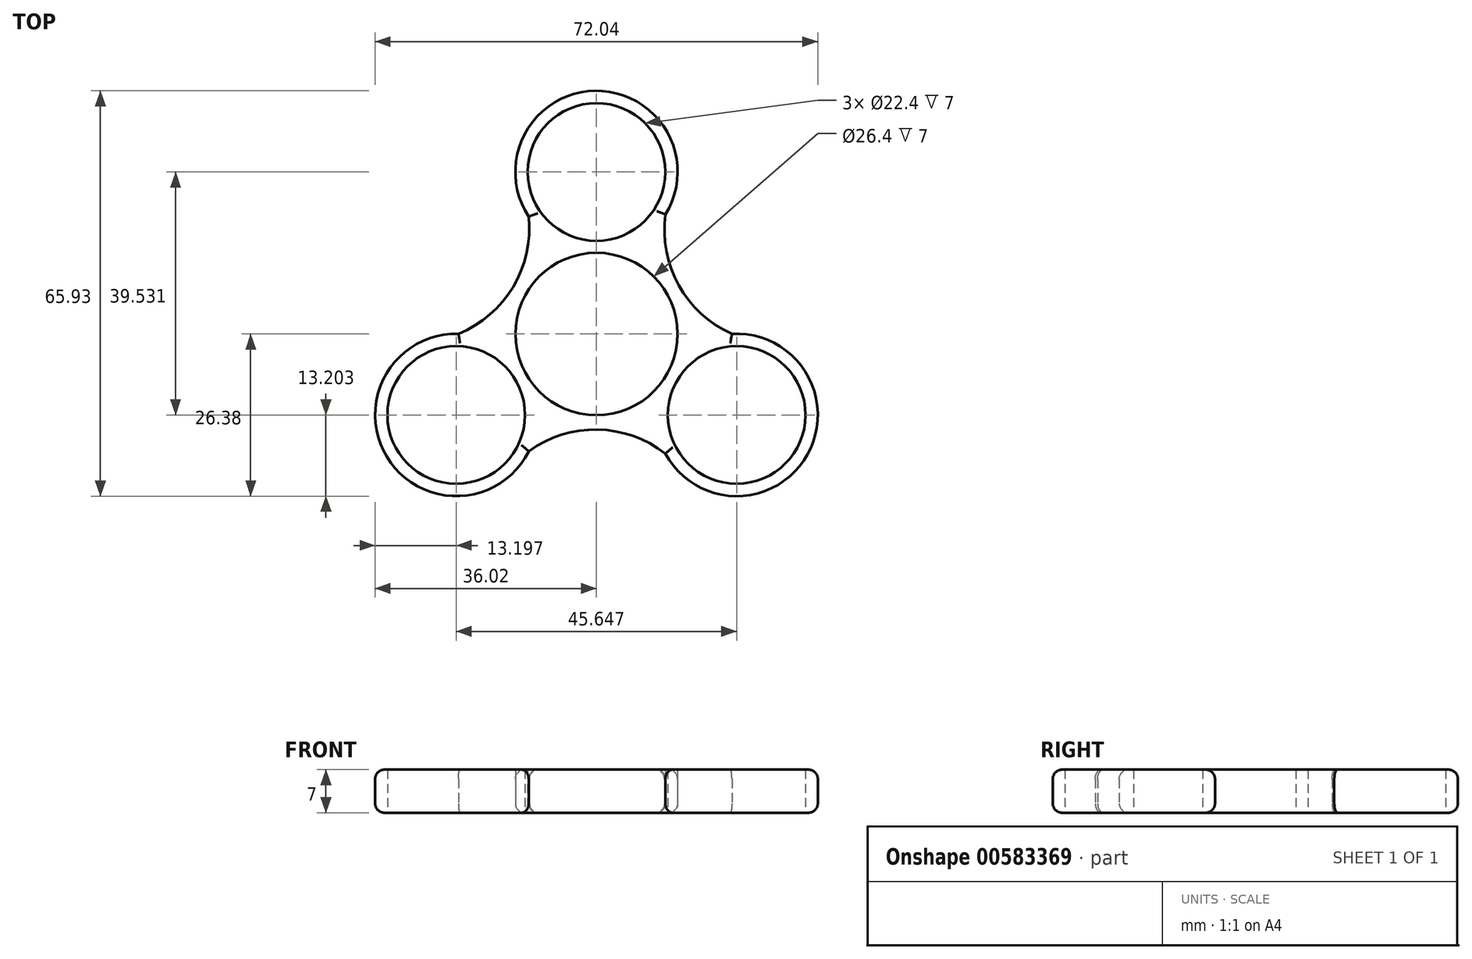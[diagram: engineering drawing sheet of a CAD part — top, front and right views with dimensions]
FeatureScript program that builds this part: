
annotation { "Feature Type Name" : "Feature", "Feature Type Description" : "" }
export const myFeature = defineFeature(function(context is Context, id is Id, definition is map)
    precondition{}
    {
        {
            var Q0;
            Q0=qCreatedBy(makeId("Top.planeOp"),FACE);
            var sketch = newSketch(context, id + "F0", { "sketchPlane" : qUnion([Q0])});
            skCircle(sketch, "E0", {"center": v(0, 0) * mm, "radius": 11.2 * mm});
            skCircle(sketch, "E1", {"center": v(0, 0) * mm, "radius": 13.2 * mm});
            skCircle(sketch, "E2", {"center": v(0, 26.35) * mm, "radius": 11.2 * mm});
            skArc(sketch, "E3", {"start": v(11.25, 19.44) * mm, "mid": v(-0.2, 39.55) * mm, "end": v(-11.02, 19.1) * mm});
            skArc(sketch, "E4.1.0", {"start": v(-22.46, 0.02) * mm, "mid": v(-34.15, -19.96) * mm, "end": v(-11.02, -19.1) * mm});
            skCircle(sketch, "E4.1.1", {"center": v(-22.82, -13.18) * mm, "radius": 11.2 * mm});
            skArc(sketch, "E4.2.0", {"start": v(11.8, -5.91) * mm, "mid": v(11.4, -6.58) * mm, "end": v(11.02, -7.26) * mm});
            skCircle(sketch, "E4.2.1", {"center": v(22.82, -13.18) * mm, "radius": 11.2 * mm});
            skLineSegment(sketch, "E5", {"start": v(-11.4, -6.64) * mm, "end": v(-11.37, -6.62) * mm});
            skArc(sketch, "E6", {"start": v(11.25, 19.44) * mm, "mid": v(13.4, 7.92) * mm, "end": v(22.04, 0) * mm});
            skArc(sketch, "E7.1.0", {"start": v(-22.46, 0.02) * mm, "mid": v(-13.56, 7.64) * mm, "end": v(-11.02, 19.1) * mm});
            skArc(sketch, "E7.2.0", {"start": v(11.22, -19.46) * mm, "mid": v(0.16, -15.56) * mm, "end": v(-11.02, -19.1) * mm});
            skArc(sketch, "E8.trimOffspring", {"start": v(11.22, -19.46) * mm, "mid": v(34.36, -19.6) * mm, "end": v(22.04, 0) * mm});
            skPoint(sketch, "E9.orphan", {"position": v(46.18, 26.35) * mm});
            skLineSegment(sketch, "E10.trimOffspring", {"start": v(11.48, 6.47) * mm, "end": v(11.5, 6.49) * mm});
            skArc(sketch, "E11.trimOffspring", {"start": v(-11.02, -7.26) * mm, "mid": v(-11.4, -6.58) * mm, "end": v(-11.8, -5.91) * mm});
            skLineSegment(sketch, "E12.trimOffspring", {"start": v(11.02, 7.26) * mm, "end": v(11.8, 5.91) * mm});
            skSolve(sketch);
        }
        {
            var Q0;
            Q0=makeQuery(id+"F0.imprint","IMPRINT",FACE,{"disambiguationData":[TD([[makeQuery(id+"F0.imprint","IMPRINT",EDGE,{"derivedFrom":sQuery(id+"F0.wireOp",EDGE,"E2")}),-1.0]])]});
            extrude(context, id + "F1", {"entities" : qUnion([Q0]), "depth" : 7 * mm, "offsetDistance" : 25 * mm});
        }
        {
            var Q0;
            Q0=makeQuery(id+"F1.opExtrude","CAP_EDGE",EDGE,{"disambiguationData":[OSD([sQuery(id+"F0.wireOp",EDGE,"E7.2.0")])],"isStart":false});
            var Q1;
            Q1=makeQuery(id+"F1.opExtrude","CAP_EDGE",EDGE,{"disambiguationData":[OSD([sQuery(id+"F0.wireOp",EDGE,"E4.1.0")])],"isStart":false});
            var Q2;
            Q2=makeQuery(id+"F1.opExtrude","CAP_EDGE",EDGE,{"disambiguationData":[OSD([sQuery(id+"F0.wireOp",EDGE,"E7.1.0")])],"isStart":false});
            var Q3;
            Q3=makeQuery(id+"F1.opExtrude","CAP_EDGE",EDGE,{"disambiguationData":[OSD([sQuery(id+"F0.wireOp",EDGE,"E3")])],"isStart":false});
            var Q4;
            Q4=makeQuery(id+"F1.opExtrude","CAP_EDGE",EDGE,{"disambiguationData":[OSD([sQuery(id+"F0.wireOp",EDGE,"E6")])],"isStart":false});
            var Q5;
            Q5=makeQuery(id+"F1.opExtrude","CAP_EDGE",EDGE,{"disambiguationData":[OSD([sQuery(id+"F0.wireOp",EDGE,"E8.trimOffspring")])],"isStart":false});
            fillet(context, id + "F2", {"entities" : qUnion([Q0, Q1, Q2, Q3, Q4, Q5]), "radius" : 1.5 * mm, "tangentPropagation" : true, "allowEdgeOverflow" : false});
        }
        {
            var Q0;
            Q0=makeQuery(id+"F1.opExtrude","CAP_EDGE",EDGE,{"disambiguationData":[OSD([sQuery(id+"F0.wireOp",EDGE,"E8.trimOffspring")])],"isStart":true});
            var Q1;
            Q1=makeQuery(id+"F1.opExtrude","CAP_EDGE",EDGE,{"disambiguationData":[OSD([sQuery(id+"F0.wireOp",EDGE,"E7.2.0")])],"isStart":true});
            var Q2;
            Q2=makeQuery(id+"F1.opExtrude","CAP_EDGE",EDGE,{"disambiguationData":[OSD([sQuery(id+"F0.wireOp",EDGE,"E4.1.0")])],"isStart":true});
            var Q3;
            Q3=makeQuery(id+"F1.opExtrude","CAP_EDGE",EDGE,{"disambiguationData":[OSD([sQuery(id+"F0.wireOp",EDGE,"E7.1.0")])],"isStart":true});
            var Q4;
            Q4=makeQuery(id+"F1.opExtrude","CAP_EDGE",EDGE,{"disambiguationData":[OSD([sQuery(id+"F0.wireOp",EDGE,"E3")])],"isStart":true});
            var Q5;
            Q5=makeQuery(id+"F1.opExtrude","CAP_EDGE",EDGE,{"disambiguationData":[OSD([sQuery(id+"F0.wireOp",EDGE,"E6")])],"isStart":true});
            fillet(context, id + "F3", {"entities" : qUnion([Q0, Q1, Q2, Q3, Q4, Q5]), "radius" : 1.5 * mm, "tangentPropagation" : true, "allowEdgeOverflow" : false});
        }
    });
